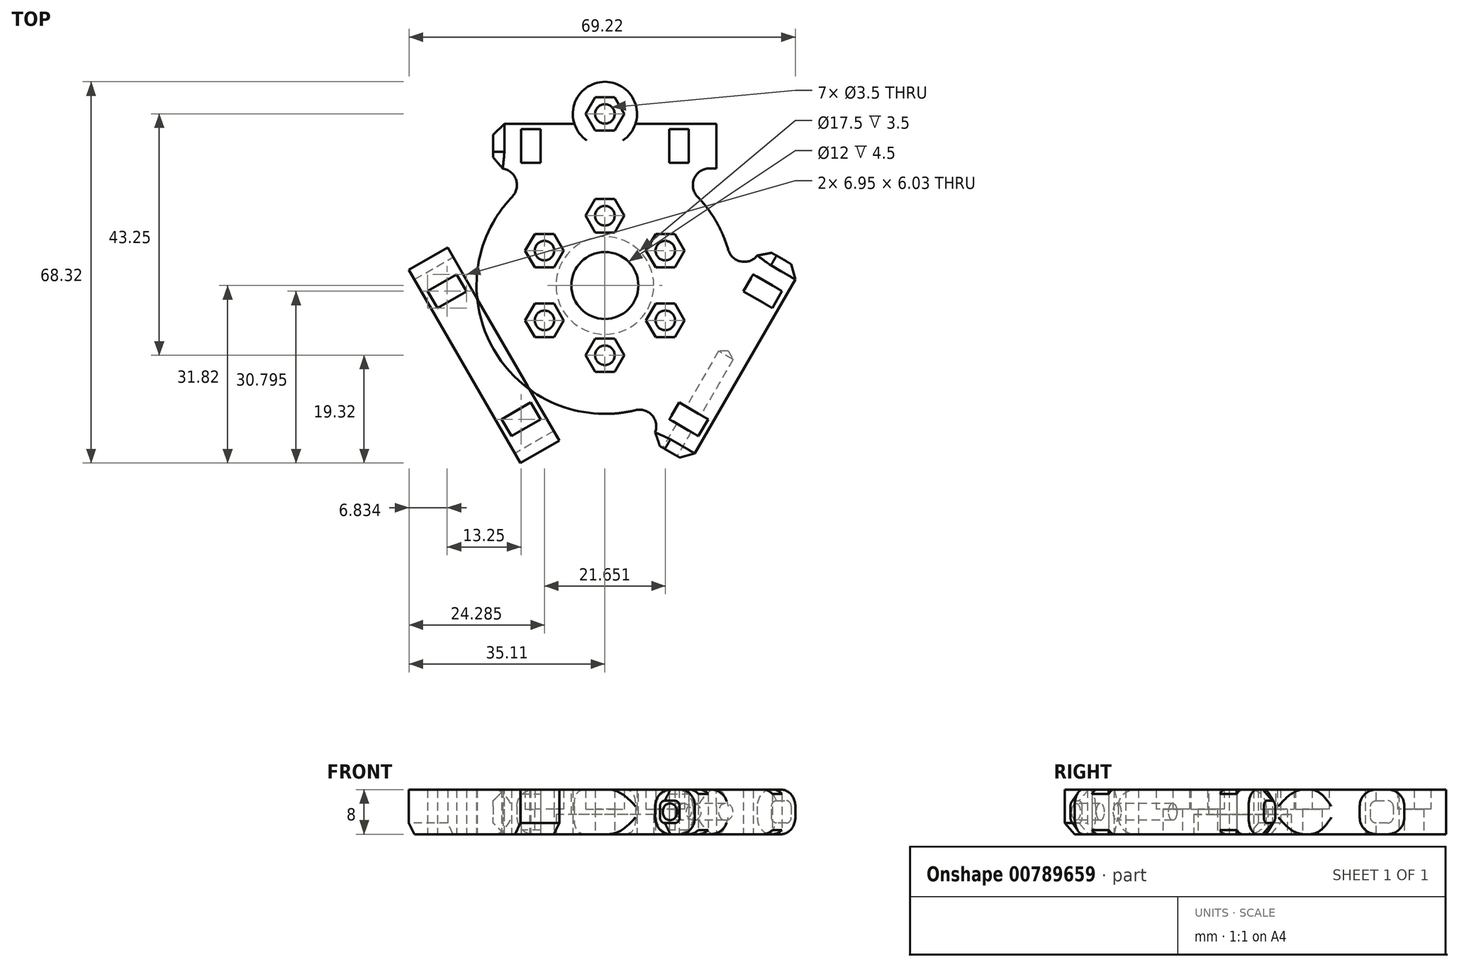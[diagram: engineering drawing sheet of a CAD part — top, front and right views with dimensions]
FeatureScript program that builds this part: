
annotation { "Feature Type Name" : "Feature", "Feature Type Description" : "" }
export const myFeature = defineFeature(function(context is Context, id is Id, definition is map)
    precondition{}
    {
        {
            var Q0;
            Q0=qCreatedBy(makeId("Front.planeOp"),FACE);
            var sketch = newSketch(context, id + "F0", { "sketchPlane" : qUnion([Q0])});
            skLineSegment(sketch, "E0", {"start": v(0, 0) * mm, "end": v(0, 21.34) * mm});
            skSolve(sketch);
        }
        {
            var Q0;
            Q0=qCreatedBy(makeId("Top.planeOp"),FACE);
            var sketch = newSketch(context, id + "F1", { "sketchPlane" : qUnion([Q0])});
            skCircle(sketch, "E1", {"center": v(0, 0) * mm, "radius": 6 * mm});
            skCircle(sketch, "E2", {"center": v(0, 0) * mm, "radius": 8.75 * mm});
            skLineSegment(sketch, "E3.bottom", {"start": v(-20, 29) * mm, "end": v(20, 29) * mm});
            skLineSegment(sketch, "E3.top", {"start": v(-20, 21) * mm, "end": v(20, 21) * mm});
            skLineSegment(sketch, "E3.left", {"start": v(-20, 29) * mm, "end": v(-20, 21) * mm});
            skLineSegment(sketch, "E3.right", {"start": v(20, 29) * mm, "end": v(20, 21) * mm});
            skLineSegment(sketch, "E4", {"start": v(-20, 25) * mm, "end": v(20, 25) * mm});
            skPoint(sketch, "E5", {"position": v(0, 25) * mm});
            skCircle(sketch, "E6.cCircle", {"center": v(0, 12.5) * mm, "radius": 3 * mm, "construction": true});
            skLineSegment(sketch, "E6.0", {"start": v(1.73, 15.5) * mm, "end": v(3.46, 12.5) * mm});
            skLineSegment(sketch, "E6.1", {"start": v(3.46, 12.5) * mm, "end": v(1.73, 9.5) * mm});
            skLineSegment(sketch, "E6.2", {"start": v(1.73, 9.5) * mm, "end": v(-1.73, 9.5) * mm});
            skLineSegment(sketch, "E6.3", {"start": v(-1.73, 9.5) * mm, "end": v(-3.46, 12.5) * mm});
            skLineSegment(sketch, "E6.4", {"start": v(-3.46, 12.5) * mm, "end": v(-1.73, 15.5) * mm});
            skLineSegment(sketch, "E6.5", {"start": v(-1.73, 15.5) * mm, "end": v(1.73, 15.5) * mm});
            skPoint(sketch, "E6.0.midPoint", {"position": v(2.6, 14) * mm});
            skLineSegment(sketch, "E7.bottom", {"start": v(-15, 22) * mm, "end": v(-11.5, 22) * mm});
            skLineSegment(sketch, "E7.top", {"start": v(-15, 28) * mm, "end": v(-11.5, 28) * mm});
            skLineSegment(sketch, "E7.left", {"start": v(-15, 22) * mm, "end": v(-15, 28) * mm});
            skLineSegment(sketch, "E7.right", {"start": v(-11.5, 22) * mm, "end": v(-11.5, 28) * mm});
            skLineSegment(sketch, "E8.bottom", {"start": v(11.5, 22) * mm, "end": v(15, 22) * mm});
            skLineSegment(sketch, "E8.top", {"start": v(11.5, 28) * mm, "end": v(15, 28) * mm});
            skLineSegment(sketch, "E8.left", {"start": v(11.5, 22) * mm, "end": v(11.5, 28) * mm});
            skLineSegment(sketch, "E8.right", {"start": v(15, 22) * mm, "end": v(15, 28) * mm});
            skCircle(sketch, "E9", {"center": v(0, 0) * mm, "radius": 23 * mm});
            skPoint(sketch, "E10", {"position": v(0, 21) * mm});
            skPoint(sketch, "E11", {"position": v(0, 23) * mm});
            skCircle(sketch, "E12", {"center": v(0, 30.75) * mm, "radius": 5.75 * mm});
            skCircle(sketch, "E13", {"center": v(0, 30.75) * mm, "radius": 1.75 * mm});
            skPoint(sketch, "E14", {"position": v(-15, 25) * mm});
            skPoint(sketch, "E15", {"position": v(15, 25) * mm});
            skLineSegment(sketch, "E16.1.0", {"start": v(24.8, -1.04) * mm, "end": v(30, -4.04) * mm});
            skLineSegment(sketch, "E16.1.1", {"start": v(31.75, -1) * mm, "end": v(30, -4.04) * mm});
            skLineSegment(sketch, "E16.1.2", {"start": v(26.55, 2) * mm, "end": v(31.75, -1) * mm});
            skLineSegment(sketch, "E16.1.3", {"start": v(26.55, 2) * mm, "end": v(24.8, -1.04) * mm});
            skLineSegment(sketch, "E16.1.4", {"start": v(13.3, -20.96) * mm, "end": v(18.5, -23.96) * mm});
            skLineSegment(sketch, "E16.1.5", {"start": v(18.5, -23.96) * mm, "end": v(16.75, -27) * mm});
            skLineSegment(sketch, "E16.1.6", {"start": v(11.55, -24) * mm, "end": v(16.75, -27) * mm});
            skLineSegment(sketch, "E16.1.7", {"start": v(13.3, -20.96) * mm, "end": v(11.55, -24) * mm});
            skLineSegment(sketch, "E16.1.8", {"start": v(31.65, 4.82) * mm, "end": v(11.65, -29.82) * mm});
            skLineSegment(sketch, "E16.1.9", {"start": v(28.19, 6.82) * mm, "end": v(8.19, -27.82) * mm});
            skLineSegment(sketch, "E16.1.10", {"start": v(35.11, 2.82) * mm, "end": v(15.11, -31.82) * mm});
            skLineSegment(sketch, "E16.1.11", {"start": v(15.11, -31.82) * mm, "end": v(8.19, -27.82) * mm});
            skLineSegment(sketch, "E16.1.12", {"start": v(35.11, 2.82) * mm, "end": v(28.19, 6.82) * mm});
            skLineSegment(sketch, "E16.2.0", {"start": v(-13.3, -20.96) * mm, "end": v(-18.5, -23.96) * mm});
            skLineSegment(sketch, "E16.2.1", {"start": v(-16.75, -27) * mm, "end": v(-18.5, -23.96) * mm});
            skLineSegment(sketch, "E16.2.2", {"start": v(-11.55, -24) * mm, "end": v(-16.75, -27) * mm});
            skLineSegment(sketch, "E16.2.3", {"start": v(-11.55, -24) * mm, "end": v(-13.3, -20.96) * mm});
            skLineSegment(sketch, "E16.2.4", {"start": v(-24.8, -1.04) * mm, "end": v(-30, -4.04) * mm});
            skLineSegment(sketch, "E16.2.5", {"start": v(-30, -4.04) * mm, "end": v(-31.75, -1) * mm});
            skLineSegment(sketch, "E16.2.6", {"start": v(-26.55, 2) * mm, "end": v(-31.75, -1) * mm});
            skLineSegment(sketch, "E16.2.7", {"start": v(-24.8, -1.04) * mm, "end": v(-26.55, 2) * mm});
            skLineSegment(sketch, "E16.2.8", {"start": v(-11.65, -29.82) * mm, "end": v(-31.65, 4.82) * mm});
            skLineSegment(sketch, "E16.2.9", {"start": v(-8.19, -27.82) * mm, "end": v(-28.19, 6.82) * mm});
            skLineSegment(sketch, "E16.2.10", {"start": v(-15.11, -31.82) * mm, "end": v(-35.11, 2.82) * mm});
            skLineSegment(sketch, "E16.2.11", {"start": v(-35.11, 2.82) * mm, "end": v(-28.19, 6.82) * mm});
            skLineSegment(sketch, "E16.2.12", {"start": v(-15.11, -31.82) * mm, "end": v(-8.19, -27.82) * mm});
            skLineSegment(sketch, "E16.anchor1", {"start": v(0, 0) * mm, "end": v(-11.5, 22) * mm, "construction": true});
            skLineSegment(sketch, "E16.anchor2", {"start": v(0, 0) * mm, "end": v(-13.3, -20.96) * mm, "construction": true});
            skCircle(sketch, "E17", {"center": v(0, 12.5) * mm, "radius": 1.75 * mm});
            skLineSegment(sketch, "E18.1.0", {"start": v(-14.29, 6.25) * mm, "end": v(-12.56, 9.25) * mm});
            skLineSegment(sketch, "E18.1.1", {"start": v(-12.56, 9.25) * mm, "end": v(-9.1, 9.25) * mm});
            skLineSegment(sketch, "E18.1.2", {"start": v(-9.1, 9.25) * mm, "end": v(-7.36, 6.25) * mm});
            skLineSegment(sketch, "E18.1.3", {"start": v(-7.36, 6.25) * mm, "end": v(-9.1, 3.25) * mm});
            skLineSegment(sketch, "E18.1.4", {"start": v(-9.1, 3.25) * mm, "end": v(-12.56, 3.25) * mm});
            skLineSegment(sketch, "E18.1.5", {"start": v(-12.56, 3.25) * mm, "end": v(-14.29, 6.25) * mm});
            skCircle(sketch, "E18.1.6", {"center": v(-10.83, 6.25) * mm, "radius": 1.75 * mm});
            skLineSegment(sketch, "E18.2.0", {"start": v(-12.56, -9.25) * mm, "end": v(-14.29, -6.25) * mm});
            skLineSegment(sketch, "E18.2.1", {"start": v(-14.29, -6.25) * mm, "end": v(-12.56, -3.25) * mm});
            skLineSegment(sketch, "E18.2.2", {"start": v(-12.56, -3.25) * mm, "end": v(-9.1, -3.25) * mm});
            skLineSegment(sketch, "E18.2.3", {"start": v(-9.1, -3.25) * mm, "end": v(-7.36, -6.25) * mm});
            skLineSegment(sketch, "E18.2.4", {"start": v(-7.36, -6.25) * mm, "end": v(-9.1, -9.25) * mm});
            skLineSegment(sketch, "E18.2.5", {"start": v(-9.1, -9.25) * mm, "end": v(-12.56, -9.25) * mm});
            skCircle(sketch, "E18.2.6", {"center": v(-10.83, -6.25) * mm, "radius": 1.75 * mm});
            skLineSegment(sketch, "E18.3.0", {"start": v(1.73, -15.5) * mm, "end": v(-1.73, -15.5) * mm});
            skLineSegment(sketch, "E18.3.1", {"start": v(-1.73, -15.5) * mm, "end": v(-3.46, -12.5) * mm});
            skLineSegment(sketch, "E18.3.2", {"start": v(-3.46, -12.5) * mm, "end": v(-1.73, -9.5) * mm});
            skLineSegment(sketch, "E18.3.3", {"start": v(-1.73, -9.5) * mm, "end": v(1.73, -9.5) * mm});
            skLineSegment(sketch, "E18.3.4", {"start": v(1.73, -9.5) * mm, "end": v(3.46, -12.5) * mm});
            skLineSegment(sketch, "E18.3.5", {"start": v(3.46, -12.5) * mm, "end": v(1.73, -15.5) * mm});
            skCircle(sketch, "E18.3.6", {"center": v(0, -12.5) * mm, "radius": 1.75 * mm});
            skLineSegment(sketch, "E18.4.0", {"start": v(14.29, -6.25) * mm, "end": v(12.56, -9.25) * mm});
            skLineSegment(sketch, "E18.4.1", {"start": v(12.56, -9.25) * mm, "end": v(9.1, -9.25) * mm});
            skLineSegment(sketch, "E18.4.2", {"start": v(9.1, -9.25) * mm, "end": v(7.36, -6.25) * mm});
            skLineSegment(sketch, "E18.4.3", {"start": v(7.36, -6.25) * mm, "end": v(9.1, -3.25) * mm});
            skLineSegment(sketch, "E18.4.4", {"start": v(9.1, -3.25) * mm, "end": v(12.56, -3.25) * mm});
            skLineSegment(sketch, "E18.4.5", {"start": v(12.56, -3.25) * mm, "end": v(14.29, -6.25) * mm});
            skCircle(sketch, "E18.4.6", {"center": v(10.83, -6.25) * mm, "radius": 1.75 * mm});
            skLineSegment(sketch, "E18.5.0", {"start": v(12.56, 9.25) * mm, "end": v(14.29, 6.25) * mm});
            skLineSegment(sketch, "E18.5.1", {"start": v(14.29, 6.25) * mm, "end": v(12.56, 3.25) * mm});
            skLineSegment(sketch, "E18.5.2", {"start": v(12.56, 3.25) * mm, "end": v(9.1, 3.25) * mm});
            skLineSegment(sketch, "E18.5.3", {"start": v(9.1, 3.25) * mm, "end": v(7.36, 6.25) * mm});
            skLineSegment(sketch, "E18.5.4", {"start": v(7.36, 6.25) * mm, "end": v(9.1, 9.25) * mm});
            skLineSegment(sketch, "E18.5.5", {"start": v(9.1, 9.25) * mm, "end": v(12.56, 9.25) * mm});
            skCircle(sketch, "E18.5.6", {"center": v(10.83, 6.25) * mm, "radius": 1.75 * mm});
            skCircle(sketch, "E19.cCircle", {"center": v(0, 30.75) * mm, "radius": 3 * mm, "construction": true});
            skLineSegment(sketch, "E19.0", {"start": v(1.73, 27.75) * mm, "end": v(-1.73, 27.75) * mm});
            skLineSegment(sketch, "E19.1", {"start": v(-1.73, 27.75) * mm, "end": v(-3.46, 30.75) * mm});
            skLineSegment(sketch, "E19.2", {"start": v(-3.46, 30.75) * mm, "end": v(-1.73, 33.75) * mm});
            skLineSegment(sketch, "E19.3", {"start": v(-1.73, 33.75) * mm, "end": v(1.73, 33.75) * mm});
            skLineSegment(sketch, "E19.4", {"start": v(1.73, 33.75) * mm, "end": v(3.46, 30.75) * mm});
            skLineSegment(sketch, "E19.5", {"start": v(3.46, 30.75) * mm, "end": v(1.73, 27.75) * mm});
            skPoint(sketch, "E19.0.midPoint", {"position": v(0, 27.75) * mm});
            skSolve(sketch);
        }
        {
            var Q0;
            Q0=makeQuery(id+"F1.imprint","IMPRINT",FACE,{"disambiguationData":[TD([[makeQuery(id+"F1.imprint","IMPRINT",EDGE,{"derivedFrom":sQuery(id+"F1.wireOp",EDGE,"E18.5.0")}),-1.0]])]});
            var Q1;
            Q1=makeQuery(id+"F1.imprint","IMPRINT",FACE,{"disambiguationData":[TD([[makeQuery(id+"F1.imprint","IMPRINT",EDGE,{"derivedFrom":sQuery(id+"F1.wireOp",EDGE,"E18.4.0")}),-1.0]])]});
            var Q2;
            Q2=makeQuery(id+"F1.imprint","IMPRINT",FACE,{"disambiguationData":[TD([[makeQuery(id+"F1.imprint","IMPRINT",EDGE,{"derivedFrom":sQuery(id+"F1.wireOp",EDGE,"E18.3.0")}),-1.0]])]});
            var Q3;
            Q3=makeQuery(id+"F1.imprint","IMPRINT",FACE,{"disambiguationData":[TD([[makeQuery(id+"F1.imprint","IMPRINT",EDGE,{"derivedFrom":sQuery(id+"F1.wireOp",EDGE,"E18.2.0")}),-1.0]])]});
            var Q4;
            Q4=makeQuery(id+"F1.imprint","IMPRINT",FACE,{"disambiguationData":[TD([[makeQuery(id+"F1.imprint","IMPRINT",EDGE,{"derivedFrom":sQuery(id+"F1.wireOp",EDGE,"E18.1.0")}),-1.0]])]});
            var Q5;
            Q5=makeQuery(id+"F1.imprint","IMPRINT",FACE,{"disambiguationData":[TD([[makeQuery(id+"F1.imprint","IMPRINT",EDGE,{"derivedFrom":sQuery(id+"F1.wireOp",EDGE,"E6.0")}),-1.0]])]});
            var Q6;
            {var subQ1=sQuery(id+"F1.wireOp",EDGE,"E19.0");Q6=makeQuery(id+"F1.imprint","IMPRINT",FACE,{"disambiguationData":[TD([[makeQuery(id+"F1.imprint","IMPRINT",EDGE,{"derivedFrom":subQ1}),-1.0]])]});}
            var Q7;
            {var subQ4=sQuery(id+"F1.wireOp",EDGE,"E13");Q7=makeQuery(id+"F1.imprint","IMPRINT",FACE,{"disambiguationData":[TD([[makeQuery(id+"F1.imprint","IMPRINT",EDGE,{"derivedFrom":subQ4}),-1.0]])]});}
            extrude(context, id + "F2", {"entities" : qUnion([Q0, Q1, Q2, Q3, Q4, Q5, Q6, Q7]), "depth" : 4.5 * mm, "offsetDistance" : 25 * mm});
        }
        {
            var Q0;
            Q0=makeQuery(id+"F1.imprint","IMPRINT",FACE,{"disambiguationData":[TD([[makeQuery(id+"F1.imprint","IMPRINT",EDGE,{"derivedFrom":sQuery(id+"F1.wireOp",EDGE,"E2")}),-1.0]])]});
            var Q1;
            {var subQ0=sQuery(id+"F1.wireOp",EDGE,"E7.bottom");Q1=makeQuery(id+"F1.imprint","IMPRINT",FACE,{"disambiguationData":[TD([[makeQuery(id+"F1.imprint","IMPRINT",EDGE,{"derivedFrom":subQ0}),-1.0]])]});}
            var Q2;
            {var subQ5=sQuery(id+"F1.wireOp",EDGE,"E7.top");Q2=makeQuery(id+"F1.imprint","IMPRINT",FACE,{"disambiguationData":[TD([[makeQuery(id+"F1.imprint","IMPRINT",EDGE,{"derivedFrom":subQ5}),1.0]])]});}
            var Q3;
            {var subQ12=sQuery(id+"F1.wireOp",EDGE,"E8.top");Q3=makeQuery(id+"F1.imprint","IMPRINT",FACE,{"disambiguationData":[TD([[makeQuery(id+"F1.imprint","IMPRINT",EDGE,{"derivedFrom":subQ12}),1.0]])]});}
            var Q4;
            {var subQ14=sQuery(id+"F1.wireOp",EDGE,"E16.1.3");Q4=makeQuery(id+"F1.imprint","IMPRINT",FACE,{"disambiguationData":[TD([[makeQuery(id+"F1.imprint","IMPRINT",EDGE,{"derivedFrom":subQ14}),-1.0]])]});}
            var Q5;
            {var subQ15=sQuery(id+"F1.wireOp",EDGE,"E16.1.1");Q5=makeQuery(id+"F1.imprint","IMPRINT",FACE,{"disambiguationData":[TD([[makeQuery(id+"F1.imprint","IMPRINT",EDGE,{"derivedFrom":subQ15}),1.0]])]});}
            var Q6;
            {var subQ0=sQuery(id+"F1.wireOp",EDGE,"E12");var subQ1=sQuery(id+"F1.wireOp",EDGE,"E3.bottom");var subQ2=makeQuery(id+"F1.imprint","INTERSECT",VERTEX,{"disambiguationData":[OD(0.0)],"derivedFrom":[subQ1,subQ0]});Q6=makeQuery(id+"F1.imprint","IMPRINT",FACE,{"disambiguationData":[TD([[makeQuery(id+"F1.imprint","IMPRINT",EDGE,{"disambiguationData":[TD([[subQ2,-1.0]])],"derivedFrom":subQ1}),-1.0]])]});}
            var Q7;
            {var subQ16=sQuery(id+"F1.wireOp",EDGE,"E16.2.3");Q7=makeQuery(id+"F1.imprint","IMPRINT",FACE,{"disambiguationData":[TD([[makeQuery(id+"F1.imprint","IMPRINT",EDGE,{"derivedFrom":subQ16}),-1.0]])]});}
            var Q8;
            {var subQ15=sQuery(id+"F1.wireOp",EDGE,"E16.2.1");Q8=makeQuery(id+"F1.imprint","IMPRINT",FACE,{"disambiguationData":[TD([[makeQuery(id+"F1.imprint","IMPRINT",EDGE,{"derivedFrom":subQ15}),1.0]])]});}
            var Q9;
            {var subQ0=sQuery(id+"F1.wireOp",EDGE,"E16.2.9");var subQ1=sQuery(id+"F1.wireOp",EDGE,"E9");var subQ2=makeQuery(id+"F1.imprint","INTERSECT",VERTEX,{"disambiguationData":[OD(0.0)],"derivedFrom":[subQ1,subQ0]});Q9=makeQuery(id+"F1.imprint","IMPRINT",FACE,{"disambiguationData":[TD([[makeQuery(id+"F1.imprint","IMPRINT",EDGE,{"disambiguationData":[TD([[subQ2,-1.0]])],"derivedFrom":subQ1}),1.0]])]});}
            var Q10;
            {var subQ0=sQuery(id+"F1.wireOp",EDGE,"E16.1.9");var subQ1=sQuery(id+"F1.wireOp",EDGE,"E9");var subQ2=makeQuery(id+"F1.imprint","INTERSECT",VERTEX,{"disambiguationData":[OD(0.0)],"derivedFrom":[subQ1,subQ0]});Q10=makeQuery(id+"F1.imprint","IMPRINT",FACE,{"disambiguationData":[TD([[makeQuery(id+"F1.imprint","IMPRINT",EDGE,{"disambiguationData":[TD([[subQ2,1.0]])],"derivedFrom":subQ1}),1.0]])]});}
            var Q11;
            {var subQ0=sQuery(id+"F1.wireOp",EDGE,"E9");var subQ1=sQuery(id+"F1.wireOp",EDGE,"E3.top");var subQ2=makeQuery(id+"F1.imprint","INTERSECT",VERTEX,{"disambiguationData":[OD(0.0)],"derivedFrom":[subQ1,subQ0]});Q11=makeQuery(id+"F1.imprint","IMPRINT",FACE,{"disambiguationData":[TD([[makeQuery(id+"F1.imprint","IMPRINT",EDGE,{"disambiguationData":[TD([[subQ2,-1.0]])],"derivedFrom":subQ1}),1.0]])]});}
            var Q12;
            {var subQ0=sQuery(id+"F1.wireOp",EDGE,"E16.1.9");var subQ1=sQuery(id+"F1.wireOp",EDGE,"E9");var subQ2=makeQuery(id+"F1.imprint","INTERSECT",VERTEX,{"disambiguationData":[OD(0.0)],"derivedFrom":[subQ1,subQ0]});Q12=makeQuery(id+"F1.imprint","IMPRINT",FACE,{"disambiguationData":[TD([[makeQuery(id+"F1.imprint","IMPRINT",EDGE,{"disambiguationData":[TD([[subQ2,-1.0]])],"derivedFrom":subQ1}),1.0]])]});}
            var Q13;
            {var subQ0=sQuery(id+"F1.wireOp",EDGE,"E19.2");Q13=makeQuery(id+"F1.imprint","IMPRINT",FACE,{"disambiguationData":[TD([[makeQuery(id+"F1.imprint","IMPRINT",EDGE,{"derivedFrom":subQ0}),1.0]])]});}
            extrude(context, id + "F3", {"entities" : qUnion([Q0, Q1, Q2, Q3, Q4, Q5, Q6, Q7, Q8, Q9, Q10, Q11, Q12, Q13]), "operationType" : NewBodyOperationType.ADD, "depth" : 8 * mm, "offsetDistance" : 25 * mm});
        }
        {
            var Q0;
            Q0=makeQuery(id+"F3.opExtrude","SWEPT_FACE",FACE,{"disambiguationData":[OSD([sQuery(id+"F1.wireOp",EDGE,"E16.2.12")])]});
            var sketch = newSketch(context, id + "F4", { "sketchPlane" : qUnion([Q0])});
            skPoint(sketch, "E20", {"position": v(-25, 4) * mm});
            skLineSegment(sketch, "E21.0.0", {"start": v(-29, 0) * mm, "end": v(-21, 0) * mm});
            skLineSegment(sketch, "E21.0.1", {"start": v(-21, 0) * mm, "end": v(-21, 8) * mm});
            skLineSegment(sketch, "E21.0.2", {"start": v(-21, 8) * mm, "end": v(-29, 8) * mm});
            skLineSegment(sketch, "E21.0.3", {"start": v(-29, 8) * mm, "end": v(-29, 0) * mm});
            skSolve(sketch);
        }
        {
            var Q0;
            Q0=makeQuery(id+"F3.opExtrude","SWEPT_FACE",FACE,{"disambiguationData":[OSD([sQuery(id+"F1.wireOp",EDGE,"E16.1.11")])]});
            var sketch = newSketch(context, id + "F5", { "sketchPlane" : qUnion([Q0])});
            skPoint(sketch, "E22", {"position": v(21, 8) * mm});
            skPoint(sketch, "E23", {"position": v(29, 0) * mm});
            skLineSegment(sketch, "E24.0.0", {"start": v(21, 0) * mm, "end": v(29, 0) * mm});
            skLineSegment(sketch, "E24.0.1", {"start": v(29, 0) * mm, "end": v(29, 8) * mm});
            skLineSegment(sketch, "E24.0.2", {"start": v(29, 8) * mm, "end": v(21, 8) * mm});
            skLineSegment(sketch, "E24.0.3", {"start": v(21, 8) * mm, "end": v(21, 0) * mm});
            skPoint(sketch, "E25", {"position": v(25, 4) * mm});
            skSolve(sketch);
        }
        {
            var Q0;
            {var subQ0=sQuery(id+"F1.wireOp",EDGE,"E16.1.9");Q0=makeQuery(id+"F3.opExtrude","CAP_EDGE",EDGE,{"disambiguationData":[OSD([subQ0]),TDD([makeQuery(id+"F1.imprint","IMPRINT",EDGE,{"disambiguationData":[TD([[makeQuery(id+"F1.imprint","INTERSECT",VERTEX,{"derivedFrom":[subQ0,sQuery(id+"F1.wireOp",EDGE,"E16.1.12")]}),-1.0]])],"derivedFrom":subQ0})])],"isStart":true});}
            var Q1;
            {var subQ0=sQuery(id+"F1.wireOp",EDGE,"E16.1.9");Q1=makeQuery(id+"F3.opExtrude","CAP_EDGE",EDGE,{"disambiguationData":[OSD([subQ0]),TDD([makeQuery(id+"F1.imprint","IMPRINT",EDGE,{"disambiguationData":[TD([[makeQuery(id+"F1.imprint","INTERSECT",VERTEX,{"derivedFrom":[subQ0,sQuery(id+"F1.wireOp",EDGE,"E16.1.12")]}),-1.0]])],"derivedFrom":subQ0})])],"isStart":false});}
            var Q2;
            Q2=makeQuery(id+"F3.opExtrude","CAP_EDGE",EDGE,{"disambiguationData":[OSD([sQuery(id+"F1.wireOp",EDGE,"E16.1.10")])],"isStart":false});
            var Q3;
            Q3=makeQuery(id+"F3.opExtrude","CAP_EDGE",EDGE,{"disambiguationData":[OSD([sQuery(id+"F1.wireOp",EDGE,"E16.1.10")])],"isStart":true});
            var Q4;
            {var subQ0=sQuery(id+"F1.wireOp",EDGE,"E16.1.9");var subQ1=sQuery(id+"F1.wireOp",EDGE,"E9");Q4=makeQuery(id+"F3.opExtrude","SWEPT_EDGE",EDGE,{"disambiguationData":[OSD([subQ1,subQ0]),TDD([makeQuery(id+"F1.imprint","INTERSECT",VERTEX,{"disambiguationData":[OD(1.0)],"derivedFrom":[subQ1,subQ0]})])]});}
            var Q5;
            {var subQ0=sQuery(id+"F1.wireOp",EDGE,"E16.1.9");var subQ1=sQuery(id+"F1.wireOp",EDGE,"E9");Q5=makeQuery(id+"F3.opExtrude","SWEPT_EDGE",EDGE,{"disambiguationData":[OSD([subQ1,subQ0]),TDD([makeQuery(id+"F1.imprint","INTERSECT",VERTEX,{"disambiguationData":[OD(0.0)],"derivedFrom":[subQ1,subQ0]})])]});}
            var Q6;
            {var subQ0=sQuery(id+"F1.wireOp",EDGE,"E16.1.9");Q6=makeQuery(id+"F3.opExtrude","CAP_EDGE",EDGE,{"disambiguationData":[OSD([subQ0]),TDD([makeQuery(id+"F1.imprint","IMPRINT",EDGE,{"disambiguationData":[TD([[makeQuery(id+"F1.imprint","INTERSECT",VERTEX,{"derivedFrom":[subQ0,sQuery(id+"F1.wireOp",EDGE,"E16.1.11")]}),1.0]])],"derivedFrom":subQ0})])],"isStart":false});}
            var Q7;
            {var subQ0=sQuery(id+"F1.wireOp",EDGE,"E16.1.9");Q7=makeQuery(id+"F3.opExtrude","CAP_EDGE",EDGE,{"disambiguationData":[OSD([subQ0]),TDD([makeQuery(id+"F1.imprint","IMPRINT",EDGE,{"disambiguationData":[TD([[makeQuery(id+"F1.imprint","INTERSECT",VERTEX,{"derivedFrom":[subQ0,sQuery(id+"F1.wireOp",EDGE,"E16.1.11")]}),1.0]])],"derivedFrom":subQ0})])],"isStart":true});}
            var Q8;
            {var subQ0=sQuery(id+"F1.wireOp",EDGE,"E16.2.9");Q8=makeQuery(id+"F3.opExtrude","CAP_EDGE",EDGE,{"disambiguationData":[OSD([subQ0]),TDD([makeQuery(id+"F1.imprint","IMPRINT",EDGE,{"disambiguationData":[TD([[makeQuery(id+"F1.imprint","INTERSECT",VERTEX,{"derivedFrom":[subQ0,sQuery(id+"F1.wireOp",EDGE,"E16.2.12")]}),-1.0]])],"derivedFrom":subQ0})])],"isStart":true});}
            var Q9;
            Q9=makeQuery(id+"F3.opExtrude","CAP_EDGE",EDGE,{"disambiguationData":[OSD([sQuery(id+"F1.wireOp",EDGE,"E16.2.10")])],"isStart":false});
            var Q10;
            Q10=makeQuery(id+"F3.opExtrude","CAP_EDGE",EDGE,{"disambiguationData":[OSD([sQuery(id+"F1.wireOp",EDGE,"E16.2.10")])],"isStart":true});
            var Q11;
            {var subQ0=sQuery(id+"F1.wireOp",EDGE,"E16.2.9");var subQ1=sQuery(id+"F1.wireOp",EDGE,"E9");Q11=makeQuery(id+"F3.opExtrude","SWEPT_EDGE",EDGE,{"disambiguationData":[OSD([subQ1,subQ0]),TDD([makeQuery(id+"F1.imprint","INTERSECT",VERTEX,{"disambiguationData":[OD(1.0)],"derivedFrom":[subQ1,subQ0]})])]});}
            var Q12;
            {var subQ0=sQuery(id+"F1.wireOp",EDGE,"E16.2.9");Q12=makeQuery(id+"F3.opExtrude","CAP_EDGE",EDGE,{"disambiguationData":[OSD([subQ0]),TDD([makeQuery(id+"F1.imprint","IMPRINT",EDGE,{"disambiguationData":[TD([[makeQuery(id+"F1.imprint","INTERSECT",VERTEX,{"derivedFrom":[subQ0,sQuery(id+"F1.wireOp",EDGE,"E16.2.12")]}),-1.0]])],"derivedFrom":subQ0})])],"isStart":false});}
            var Q13;
            {var subQ0=sQuery(id+"F1.wireOp",EDGE,"E16.2.9");Q13=makeQuery(id+"F3.opExtrude","CAP_EDGE",EDGE,{"disambiguationData":[OSD([subQ0]),TDD([makeQuery(id+"F1.imprint","IMPRINT",EDGE,{"disambiguationData":[TD([[makeQuery(id+"F1.imprint","INTERSECT",VERTEX,{"derivedFrom":[subQ0,sQuery(id+"F1.wireOp",EDGE,"E16.2.11")]}),1.0]])],"derivedFrom":subQ0})])],"isStart":false});}
            var Q14;
            {var subQ0=sQuery(id+"F1.wireOp",EDGE,"E3.top");Q14=makeQuery(id+"F3.opExtrude","CAP_EDGE",EDGE,{"disambiguationData":[OSD([subQ0]),TDD([makeQuery(id+"F1.imprint","IMPRINT",EDGE,{"disambiguationData":[TD([[makeQuery(id+"F1.imprint","INTERSECT",VERTEX,{"derivedFrom":[subQ0,sQuery(id+"F1.wireOp",EDGE,"E3.right")]}),1.0]])],"derivedFrom":subQ0})])],"isStart":true});}
            var Q15;
            {var subQ0=sQuery(id+"F1.wireOp",EDGE,"E3.top");Q15=makeQuery(id+"F3.opExtrude","CAP_EDGE",EDGE,{"disambiguationData":[OSD([subQ0]),TDD([makeQuery(id+"F1.imprint","IMPRINT",EDGE,{"disambiguationData":[TD([[makeQuery(id+"F1.imprint","INTERSECT",VERTEX,{"derivedFrom":[subQ0,sQuery(id+"F1.wireOp",EDGE,"E3.right")]}),1.0]])],"derivedFrom":subQ0})])],"isStart":false});}
            var Q16;
            {var subQ0=sQuery(id+"F1.wireOp",EDGE,"E3.top");Q16=makeQuery(id+"F3.opExtrude","CAP_EDGE",EDGE,{"disambiguationData":[OSD([subQ0]),TDD([makeQuery(id+"F1.imprint","IMPRINT",EDGE,{"disambiguationData":[TD([[makeQuery(id+"F1.imprint","INTERSECT",VERTEX,{"derivedFrom":[subQ0,sQuery(id+"F1.wireOp",EDGE,"E3.left")]}),-1.0]])],"derivedFrom":subQ0})])],"isStart":false});}
            var Q17;
            {var subQ0=sQuery(id+"F1.wireOp",EDGE,"E9");var subQ1=sQuery(id+"F1.wireOp",EDGE,"E3.top");Q17=makeQuery(id+"F3.opExtrude","SWEPT_EDGE",EDGE,{"disambiguationData":[OSD([subQ1,subQ0]),TDD([makeQuery(id+"F1.imprint","INTERSECT",VERTEX,{"disambiguationData":[OD(0.0)],"derivedFrom":[subQ1,subQ0]})])]});}
            var Q18;
            {var subQ0=sQuery(id+"F1.wireOp",EDGE,"E3.top");Q18=makeQuery(id+"F3.opExtrude","CAP_EDGE",EDGE,{"disambiguationData":[OSD([subQ0]),TDD([makeQuery(id+"F1.imprint","IMPRINT",EDGE,{"disambiguationData":[TD([[makeQuery(id+"F1.imprint","INTERSECT",VERTEX,{"derivedFrom":[subQ0,sQuery(id+"F1.wireOp",EDGE,"E3.left")]}),-1.0]])],"derivedFrom":subQ0})])],"isStart":true});}
            var Q19;
            {var subQ0=sQuery(id+"F1.wireOp",EDGE,"E3.bottom");Q19=makeQuery(id+"F3.opExtrude","CAP_EDGE",EDGE,{"disambiguationData":[OSD([subQ0]),TDD([makeQuery(id+"F1.imprint","IMPRINT",EDGE,{"disambiguationData":[TD([[makeQuery(id+"F1.imprint","INTERSECT",VERTEX,{"derivedFrom":[subQ0,sQuery(id+"F1.wireOp",EDGE,"E3.left")]}),-1.0]])],"derivedFrom":subQ0})])],"isStart":true});}
            var Q20;
            {var subQ0=sQuery(id+"F1.wireOp",EDGE,"E3.bottom");Q20=makeQuery(id+"F3.opExtrude","CAP_EDGE",EDGE,{"disambiguationData":[OSD([subQ0]),TDD([makeQuery(id+"F1.imprint","IMPRINT",EDGE,{"disambiguationData":[TD([[makeQuery(id+"F1.imprint","INTERSECT",VERTEX,{"derivedFrom":[subQ0,sQuery(id+"F1.wireOp",EDGE,"E3.left")]}),-1.0]])],"derivedFrom":subQ0})])],"isStart":false});}
            var Q21;
            {var subQ0=sQuery(id+"F1.wireOp",EDGE,"E3.bottom");Q21=makeQuery(id+"F3.opExtrude","CAP_EDGE",EDGE,{"disambiguationData":[OSD([subQ0]),TDD([makeQuery(id+"F1.imprint","IMPRINT",EDGE,{"disambiguationData":[TD([[makeQuery(id+"F1.imprint","INTERSECT",VERTEX,{"derivedFrom":[subQ0,sQuery(id+"F1.wireOp",EDGE,"E3.right")]}),1.0]])],"derivedFrom":subQ0})])],"isStart":true});}
            var Q22;
            {var subQ0=sQuery(id+"F1.wireOp",EDGE,"E3.bottom");Q22=makeQuery(id+"F3.opExtrude","CAP_EDGE",EDGE,{"disambiguationData":[OSD([subQ0]),TDD([makeQuery(id+"F1.imprint","IMPRINT",EDGE,{"disambiguationData":[TD([[makeQuery(id+"F1.imprint","INTERSECT",VERTEX,{"derivedFrom":[subQ0,sQuery(id+"F1.wireOp",EDGE,"E3.right")]}),1.0]])],"derivedFrom":subQ0})])],"isStart":false});}
            var Q23;
            {var subQ0=sQuery(id+"F1.wireOp",EDGE,"E16.2.9");Q23=makeQuery(id+"F3.opExtrude","CAP_EDGE",EDGE,{"disambiguationData":[OSD([subQ0]),TDD([makeQuery(id+"F1.imprint","IMPRINT",EDGE,{"disambiguationData":[TD([[makeQuery(id+"F1.imprint","INTERSECT",VERTEX,{"derivedFrom":[subQ0,sQuery(id+"F1.wireOp",EDGE,"E16.2.11")]}),1.0]])],"derivedFrom":subQ0})])],"isStart":true});}
            var Q24;
            {var subQ0=sQuery(id+"F1.wireOp",EDGE,"E16.2.9");var subQ1=sQuery(id+"F1.wireOp",EDGE,"E9");Q24=makeQuery(id+"F3.opExtrude","SWEPT_EDGE",EDGE,{"disambiguationData":[OSD([subQ1,subQ0]),TDD([makeQuery(id+"F1.imprint","INTERSECT",VERTEX,{"disambiguationData":[OD(0.0)],"derivedFrom":[subQ1,subQ0]})])]});}
            var Q25;
            {var subQ0=sQuery(id+"F1.wireOp",EDGE,"E9");var subQ1=sQuery(id+"F1.wireOp",EDGE,"E3.top");Q25=makeQuery(id+"F3.opExtrude","SWEPT_EDGE",EDGE,{"disambiguationData":[OSD([subQ1,subQ0]),TDD([makeQuery(id+"F1.imprint","INTERSECT",VERTEX,{"disambiguationData":[OD(1.0)],"derivedFrom":[subQ1,subQ0]})])]});}
            fillet(context, id + "F6", {"entities" : qUnion([Q0, Q1, Q2, Q3, Q4, Q5, Q6, Q7, Q8, Q9, Q10, Q11, Q12, Q13, Q14, Q15, Q16, Q17, Q18, Q19, Q20, Q21, Q22, Q23, Q24, Q25]), "radius" : 3 * mm, "allowEdgeOverflow" : false});
        }
        {
            var Q0;
            Q0=sQuery(id+"F5.wireOp",VERTEX,"E25");
            var Q1;
            Q1=sQuery(id+"F4.wireOp",VERTEX,"E20");
            var Q2;
            Q2=makeQuery(id+"F2.opExtrude","SWEPT_BODY",BODY,{"disambiguationData":[OSD([sQuery(id+"F1.wireOp",EDGE,"E6.0"),sQuery(id+"F1.wireOp",EDGE,"E6.1"),sQuery(id+"F1.wireOp",EDGE,"E6.2"),sQuery(id+"F1.wireOp",EDGE,"E6.3"),sQuery(id+"F1.wireOp",EDGE,"E6.4"),sQuery(id+"F1.wireOp",EDGE,"E6.5"),sQuery(id+"F1.wireOp",EDGE,"E17")])]});
            hole(context, id + "F7", {"style" : HoleStyle.C_SINK, "endStyle" : HoleEndStyle.BLIND, "holeDiameter" : 3 * mm, "cSinkDiameter" : 3 * mm, "cSinkAngle" : 90 * degree, "majorDiameter" : 5 * mm, "holeDepth" : 20 * mm, "isTappedThrough" : true, "tappedDepth" : 12 * mm, "tapClearance" : 3, "locations" : qUnion([Q0, Q1]), "scope" : qUnion([Q2])});
        }
        {
            var Q0;
            Q0=makeQuery(id+"F6.opFillet","SPLIT",FACE,{"disambiguationData":[OD(6.0)],"derivedFrom":makeQuery(id+"F3.opExtrude","CAP_FACE",FACE,{"disambiguationData":[OSD([sQuery(id+"F1.wireOp",EDGE,"E2"),sQuery(id+"F1.wireOp",EDGE,"E3.bottom"),sQuery(id+"F1.wireOp",EDGE,"E3.top"),sQuery(id+"F1.wireOp",EDGE,"E3.left"),sQuery(id+"F1.wireOp",EDGE,"E3.right"),sQuery(id+"F1.wireOp",EDGE,"E6.0"),sQuery(id+"F1.wireOp",EDGE,"E6.1"),sQuery(id+"F1.wireOp",EDGE,"E6.2"),sQuery(id+"F1.wireOp",EDGE,"E6.3"),sQuery(id+"F1.wireOp",EDGE,"E6.4"),sQuery(id+"F1.wireOp",EDGE,"E6.5"),sQuery(id+"F1.wireOp",EDGE,"E7.bottom"),sQuery(id+"F1.wireOp",EDGE,"E7.top"),sQuery(id+"F1.wireOp",EDGE,"E7.left"),sQuery(id+"F1.wireOp",EDGE,"E7.right"),sQuery(id+"F1.wireOp",EDGE,"E8.bottom"),sQuery(id+"F1.wireOp",EDGE,"E8.top"),sQuery(id+"F1.wireOp",EDGE,"E8.left"),sQuery(id+"F1.wireOp",EDGE,"E8.right"),sQuery(id+"F1.wireOp",EDGE,"E9"),sQuery(id+"F1.wireOp",EDGE,"E12"),sQuery(id+"F1.wireOp",EDGE,"E16.1.0"),sQuery(id+"F1.wireOp",EDGE,"E16.1.1"),sQuery(id+"F1.wireOp",EDGE,"E16.1.2"),sQuery(id+"F1.wireOp",EDGE,"E16.1.3"),sQuery(id+"F1.wireOp",EDGE,"E16.1.4"),sQuery(id+"F1.wireOp",EDGE,"E16.1.5"),sQuery(id+"F1.wireOp",EDGE,"E16.1.6"),sQuery(id+"F1.wireOp",EDGE,"E16.1.7"),sQuery(id+"F1.wireOp",EDGE,"E16.1.9"),sQuery(id+"F1.wireOp",EDGE,"E16.1.10"),sQuery(id+"F1.wireOp",EDGE,"E16.1.11"),sQuery(id+"F1.wireOp",EDGE,"E16.1.12"),sQuery(id+"F1.wireOp",EDGE,"E16.2.0"),sQuery(id+"F1.wireOp",EDGE,"E16.2.1"),sQuery(id+"F1.wireOp",EDGE,"E16.2.2"),sQuery(id+"F1.wireOp",EDGE,"E16.2.3"),sQuery(id+"F1.wireOp",EDGE,"E16.2.4"),sQuery(id+"F1.wireOp",EDGE,"E16.2.5"),sQuery(id+"F1.wireOp",EDGE,"E16.2.6"),sQuery(id+"F1.wireOp",EDGE,"E16.2.7"),sQuery(id+"F1.wireOp",EDGE,"E16.2.9"),sQuery(id+"F1.wireOp",EDGE,"E16.2.10"),sQuery(id+"F1.wireOp",EDGE,"E16.2.11"),sQuery(id+"F1.wireOp",EDGE,"E16.2.12"),sQuery(id+"F1.wireOp",EDGE,"E18.1.0"),sQuery(id+"F1.wireOp",EDGE,"E18.1.1"),sQuery(id+"F1.wireOp",EDGE,"E18.1.2"),sQuery(id+"F1.wireOp",EDGE,"E18.1.3"),sQuery(id+"F1.wireOp",EDGE,"E18.1.4"),sQuery(id+"F1.wireOp",EDGE,"E18.1.5"),sQuery(id+"F1.wireOp",EDGE,"E18.2.0"),sQuery(id+"F1.wireOp",EDGE,"E18.2.1"),sQuery(id+"F1.wireOp",EDGE,"E18.2.2"),sQuery(id+"F1.wireOp",EDGE,"E18.2.3"),sQuery(id+"F1.wireOp",EDGE,"E18.2.4"),sQuery(id+"F1.wireOp",EDGE,"E18.2.5"),sQuery(id+"F1.wireOp",EDGE,"E18.3.0"),sQuery(id+"F1.wireOp",EDGE,"E18.3.1"),sQuery(id+"F1.wireOp",EDGE,"E18.3.2"),sQuery(id+"F1.wireOp",EDGE,"E18.3.3"),sQuery(id+"F1.wireOp",EDGE,"E18.3.4"),sQuery(id+"F1.wireOp",EDGE,"E18.3.5"),sQuery(id+"F1.wireOp",EDGE,"E18.4.0"),sQuery(id+"F1.wireOp",EDGE,"E18.4.1"),sQuery(id+"F1.wireOp",EDGE,"E18.4.2"),sQuery(id+"F1.wireOp",EDGE,"E18.4.3"),sQuery(id+"F1.wireOp",EDGE,"E18.4.4"),sQuery(id+"F1.wireOp",EDGE,"E18.4.5"),sQuery(id+"F1.wireOp",EDGE,"E18.5.0"),sQuery(id+"F1.wireOp",EDGE,"E18.5.1"),sQuery(id+"F1.wireOp",EDGE,"E18.5.2"),sQuery(id+"F1.wireOp",EDGE,"E18.5.3"),sQuery(id+"F1.wireOp",EDGE,"E18.5.4"),sQuery(id+"F1.wireOp",EDGE,"E18.5.5"),sQuery(id+"F1.wireOp",EDGE,"E19.0"),sQuery(id+"F1.wireOp",EDGE,"E19.1"),sQuery(id+"F1.wireOp",EDGE,"E19.2"),sQuery(id+"F1.wireOp",EDGE,"E19.3"),sQuery(id+"F1.wireOp",EDGE,"E19.4"),sQuery(id+"F1.wireOp",EDGE,"E19.5")])],"isStart":false})});
            var sketch = newSketch(context, id + "F8", { "sketchPlane" : qUnion([Q0])});
            skCircle(sketch, "E26.0", {"center": v(0, 0) * mm, "radius": 6 * mm});
            skCircle(sketch, "E27.0", {"center": v(0, 0) * mm, "radius": 8.75 * mm});
            skSolve(sketch);
        }
        {
            var Q0;
            Q0=makeQuery(id+"F8.imprint","IMPRINT",FACE,{"disambiguationData":[TD([[makeQuery(id+"F8.imprint","IMPRINT",EDGE,{"derivedFrom":sQuery(id+"F8.wireOp",EDGE,"E26.0")}),-1.0]])]});
            extrude(context, id + "F9", {"entities" : qUnion([Q0]), "operationType" : NewBodyOperationType.ADD, "oppositeDirection" : true, "depth" : 4.5 * mm, "offsetDistance" : 25 * mm});
        }
        {
            var Q0;
            Q0=makeQuery(id+"F3.opExtrude","CAP_EDGE",EDGE,{"disambiguationData":[OSD([sQuery(id+"F1.wireOp",EDGE,"E16.2.11")])],"isStart":true});
            var Q1;
            Q1=makeQuery(id+"F3.opExtrude","CAP_EDGE",EDGE,{"disambiguationData":[OSD([sQuery(id+"F1.wireOp",EDGE,"E16.2.12")])],"isStart":true});
            var Q2;
            Q2=makeQuery(id+"F3.opExtrude","CAP_EDGE",EDGE,{"disambiguationData":[OSD([sQuery(id+"F1.wireOp",EDGE,"E16.1.11")])],"isStart":true});
            var Q3;
            Q3=makeQuery(id+"F3.opExtrude","CAP_EDGE",EDGE,{"disambiguationData":[OSD([sQuery(id+"F1.wireOp",EDGE,"E3.left")])],"isStart":true});
            var Q4;
            Q4=makeQuery(id+"F3.opExtrude","CAP_EDGE",EDGE,{"disambiguationData":[OSD([sQuery(id+"F1.wireOp",EDGE,"E16.1.12")])],"isStart":true});
            chamfer(context, id + "F10", {"entities" : qUnion([Q0, Q1, Q2, Q3, Q4]), "width" : 2 * mm, "tangentPropagation" : true});
        }
    });
